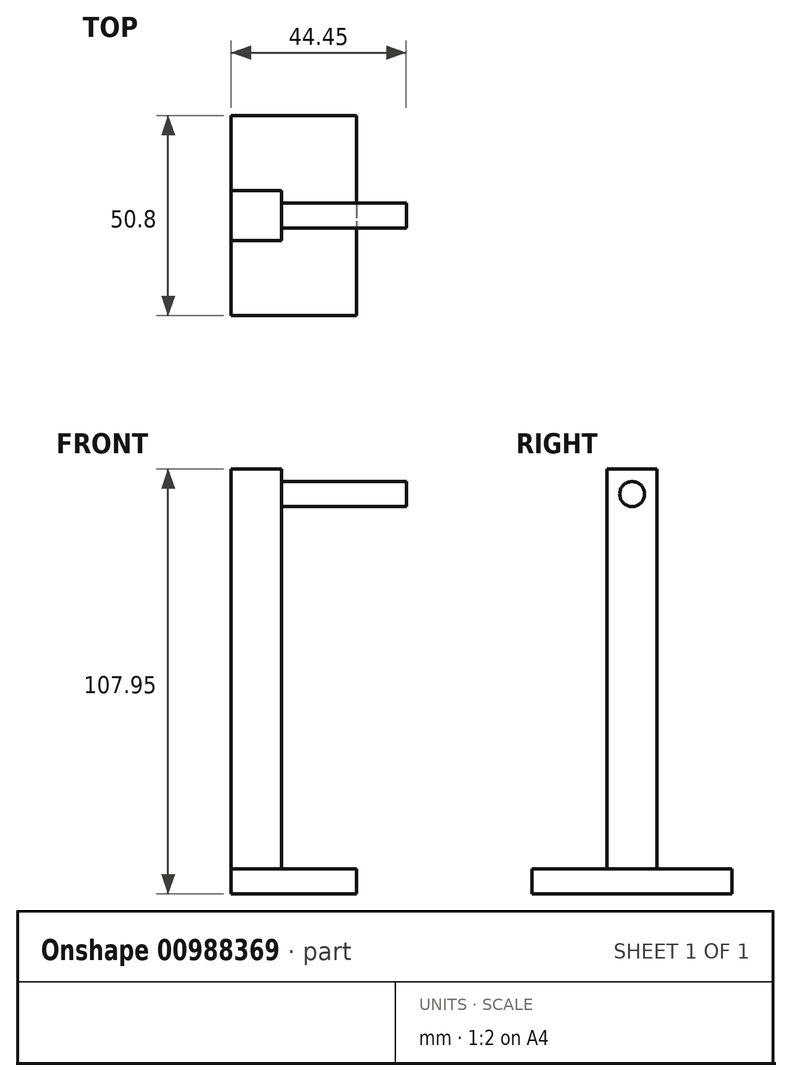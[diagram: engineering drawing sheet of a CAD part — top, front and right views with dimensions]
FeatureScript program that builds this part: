
annotation { "Feature Type Name" : "Feature", "Feature Type Description" : "" }
export const myFeature = defineFeature(function(context is Context, id is Id, definition is map)
    precondition{}
    {
        {
            var Q0;
            Q0=qCreatedBy(makeId("Top.planeOp"),FACE);
            var sketch = newSketch(context, id + "F0", { "sketchPlane" : qUnion([Q0])});
            skLineSegment(sketch, "E0.bottom", {"start": v(-25.69, 25.3) * mm, "end": v(25.11, 25.3) * mm});
            skLineSegment(sketch, "E0.top", {"start": v(-25.69, -25.5) * mm, "end": v(25.11, -25.5) * mm});
            skLineSegment(sketch, "E0.left", {"start": v(-25.69, 25.3) * mm, "end": v(-25.69, -25.5) * mm});
            skLineSegment(sketch, "E0.right", {"start": v(25.11, 25.3) * mm, "end": v(25.11, -25.5) * mm});
            skSolve(sketch);
        }
        {
            var Q0;
            Q0=makeQuery(id+"F0.imprint","IMPRINT",FACE,{"disambiguationData":[TD([[makeQuery(id+"F0.imprint","IMPRINT",EDGE,{"derivedFrom":sQuery(id+"F0.wireOp",EDGE,"E0.bottom")}),-1.0]])]});
            extrude(context, id + "F1", {"entities" : qUnion([Q0]), "depth" : 6.35 * mm, "offsetDistance" : 25.4 * mm});
        }
        {
            var Q0;
            Q0=makeQuery(id+"F1.opExtrude","CAP_FACE",FACE,{"disambiguationData":[OSD([sQuery(id+"F0.wireOp",EDGE,"E0.bottom"),sQuery(id+"F0.wireOp",EDGE,"E0.top"),sQuery(id+"F0.wireOp",EDGE,"E0.left"),sQuery(id+"F0.wireOp",EDGE,"E0.right")])],"isStart":false});
            var sketch = newSketch(context, id + "F2", { "sketchPlane" : qUnion([Q0])});
            skLineSegment(sketch, "E1", {"start": v(-25.69, 25.3) * mm, "end": v(25.11, -25.5) * mm, "construction": true});
            skLineSegment(sketch, "E2", {"start": v(25.11, 25.3) * mm, "end": v(-25.69, -25.5) * mm, "construction": true});
            skLineSegment(sketch, "E3.bottom", {"start": v(6.06, 6.25) * mm, "end": v(-6.64, 6.25) * mm});
            skLineSegment(sketch, "E3.top", {"start": v(6.06, -6.45) * mm, "end": v(-6.64, -6.45) * mm});
            skLineSegment(sketch, "E3.left", {"start": v(6.06, 6.25) * mm, "end": v(6.06, -6.45) * mm});
            skLineSegment(sketch, "E3.right", {"start": v(-6.64, 6.25) * mm, "end": v(-6.64, -6.45) * mm});
            skPoint(sketch, "E3.middle", {"position": v(-0.29, -0.1) * mm});
            skSolve(sketch);
        }
        {
            var Q0;
            Q0=makeQuery(id+"F2.imprint","IMPRINT",FACE,{"disambiguationData":[TD([[makeQuery(id+"F2.imprint","IMPRINT",EDGE,{"derivedFrom":sQuery(id+"F2.wireOp",EDGE,"E3.bottom")}),1.0]])]});
            extrude(context, id + "F3", {"entities" : qUnion([Q0]), "operationType" : NewBodyOperationType.ADD, "depth" : 101.6 * mm, "offsetDistance" : 25.4 * mm});
        }
        {
            var Q0;
            Q0=makeQuery(id+"F3.opExtrude","SWEPT_FACE",FACE,{"disambiguationData":[OSD([sQuery(id+"F2.wireOp",EDGE,"E3.left")])]});
            var sketch = newSketch(context, id + "F4", { "sketchPlane" : qUnion([Q0])});
            skLineSegment(sketch, "E4", {"start": v(-6.45, 107.95) * mm, "end": v(6.25, 95.25) * mm, "construction": true});
            skLineSegment(sketch, "E5", {"start": v(6.25, 95.25) * mm, "end": v(6.25, 107.95) * mm, "construction": true});
            skLineSegment(sketch, "E6", {"start": v(6.25, 107.95) * mm, "end": v(-6.45, 95.25) * mm, "construction": true});
            skLineSegment(sketch, "E7", {"start": v(-6.45, 95.25) * mm, "end": v(-6.45, 107.95) * mm, "construction": true});
            skCircle(sketch, "E8", {"center": v(-0.1, 101.6) * mm, "radius": 3.18 * mm});
            skSolve(sketch);
        }
        {
            var Q0;
            Q0=makeQuery(id+"F4.imprint","IMPRINT",FACE,{"disambiguationData":[TD([[makeQuery(id+"F4.imprint","IMPRINT",EDGE,{"derivedFrom":sQuery(id+"F4.wireOp",EDGE,"E8")}),1.0]])]});
            extrude(context, id + "F5", {"entities" : qUnion([Q0]), "operationType" : NewBodyOperationType.ADD, "depth" : 31.75 * mm, "offsetDistance" : 25.4 * mm});
        }
        {
            var Q0;
            Q0=makeQuery(id+"F1.opExtrude","CAP_FACE",FACE,{"disambiguationData":[OSD([sQuery(id+"F0.wireOp",EDGE,"E0.bottom"),sQuery(id+"F0.wireOp",EDGE,"E0.top"),sQuery(id+"F0.wireOp",EDGE,"E0.left"),sQuery(id+"F0.wireOp",EDGE,"E0.right")])],"isStart":false});
            var sketch = newSketch(context, id + "F6", { "sketchPlane" : qUnion([Q0])});
            skLineSegment(sketch, "E9", {"start": v(-6.64, 6.25) * mm, "end": v(-6.64, -6.45) * mm});
            skLineSegment(sketch, "E10", {"start": v(-6.64, -6.45) * mm, "end": v(-6.64, -25.5) * mm});
            skLineSegment(sketch, "E11", {"start": v(-6.64, -25.5) * mm, "end": v(-25.69, -25.5) * mm});
            skLineSegment(sketch, "E12", {"start": v(-25.69, -25.5) * mm, "end": v(-25.69, 25.3) * mm});
            skLineSegment(sketch, "E13", {"start": v(-25.69, 25.3) * mm, "end": v(-6.64, 25.3) * mm});
            skLineSegment(sketch, "E14", {"start": v(-6.64, 25.3) * mm, "end": v(-6.64, 6.25) * mm});
            skSolve(sketch);
        }
        {
            var Q0;
            Q0=makeQuery(id+"F6.imprint","IMPRINT",FACE,{"disambiguationData":[TD([[makeQuery(id+"F6.imprint","IMPRINT",EDGE,{"derivedFrom":sQuery(id+"F6.wireOp",EDGE,"E9")}),-1.0]])]});
            extrude(context, id + "F7", {"entities" : qUnion([Q0]), "operationType" : NewBodyOperationType.REMOVE, "oppositeDirection" : true, "depth" : 25.4 * mm, "offsetDistance" : 25.4 * mm});
        }
    });
